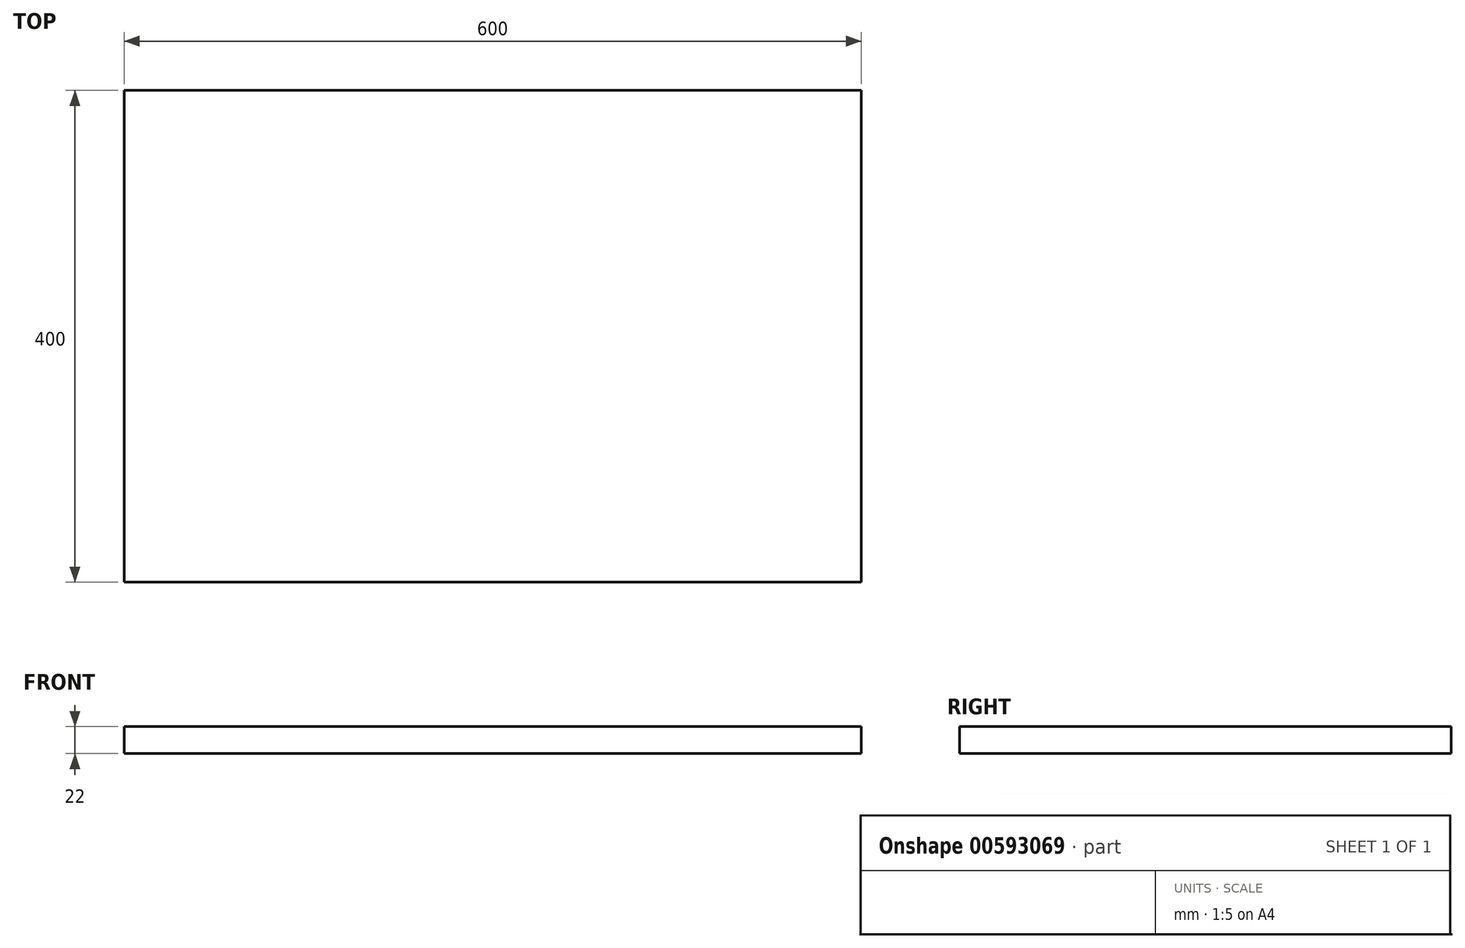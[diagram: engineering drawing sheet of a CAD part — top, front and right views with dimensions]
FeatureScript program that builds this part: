
annotation { "Feature Type Name" : "Feature", "Feature Type Description" : "" }
export const myFeature = defineFeature(function(context is Context, id is Id, definition is map)
    precondition{}
    {
        {
            var Q0;
            Q0=qCreatedBy(makeId("Top.planeOp"),FACE);
            var sketch = newSketch(context, id + "F0", { "sketchPlane" : qUnion([Q0])});
            skLineSegment(sketch, "E0.bottom", {"start": v(-300, 200) * mm, "end": v(300, 200) * mm});
            skLineSegment(sketch, "E0.top", {"start": v(-300, -200) * mm, "end": v(300, -200) * mm});
            skLineSegment(sketch, "E0.left", {"start": v(-300, 200) * mm, "end": v(-300, -200) * mm});
            skLineSegment(sketch, "E0.right", {"start": v(300, 200) * mm, "end": v(300, -200) * mm});
            skSolve(sketch);
        }
        {
            var Q0;
            Q0=makeQuery(id+"F0.imprint","IMPRINT",FACE,{"disambiguationData":[TD([[makeQuery(id+"F0.imprint","IMPRINT",EDGE,{"derivedFrom":sQuery(id+"F0.wireOp",EDGE,"E0.bottom")}),-1.0]])]});
            extrude(context, id + "F1", {"entities" : qUnion([Q0]), "depth" : 22 * mm, "offsetDistance" : 25 * mm});
        }
    });
